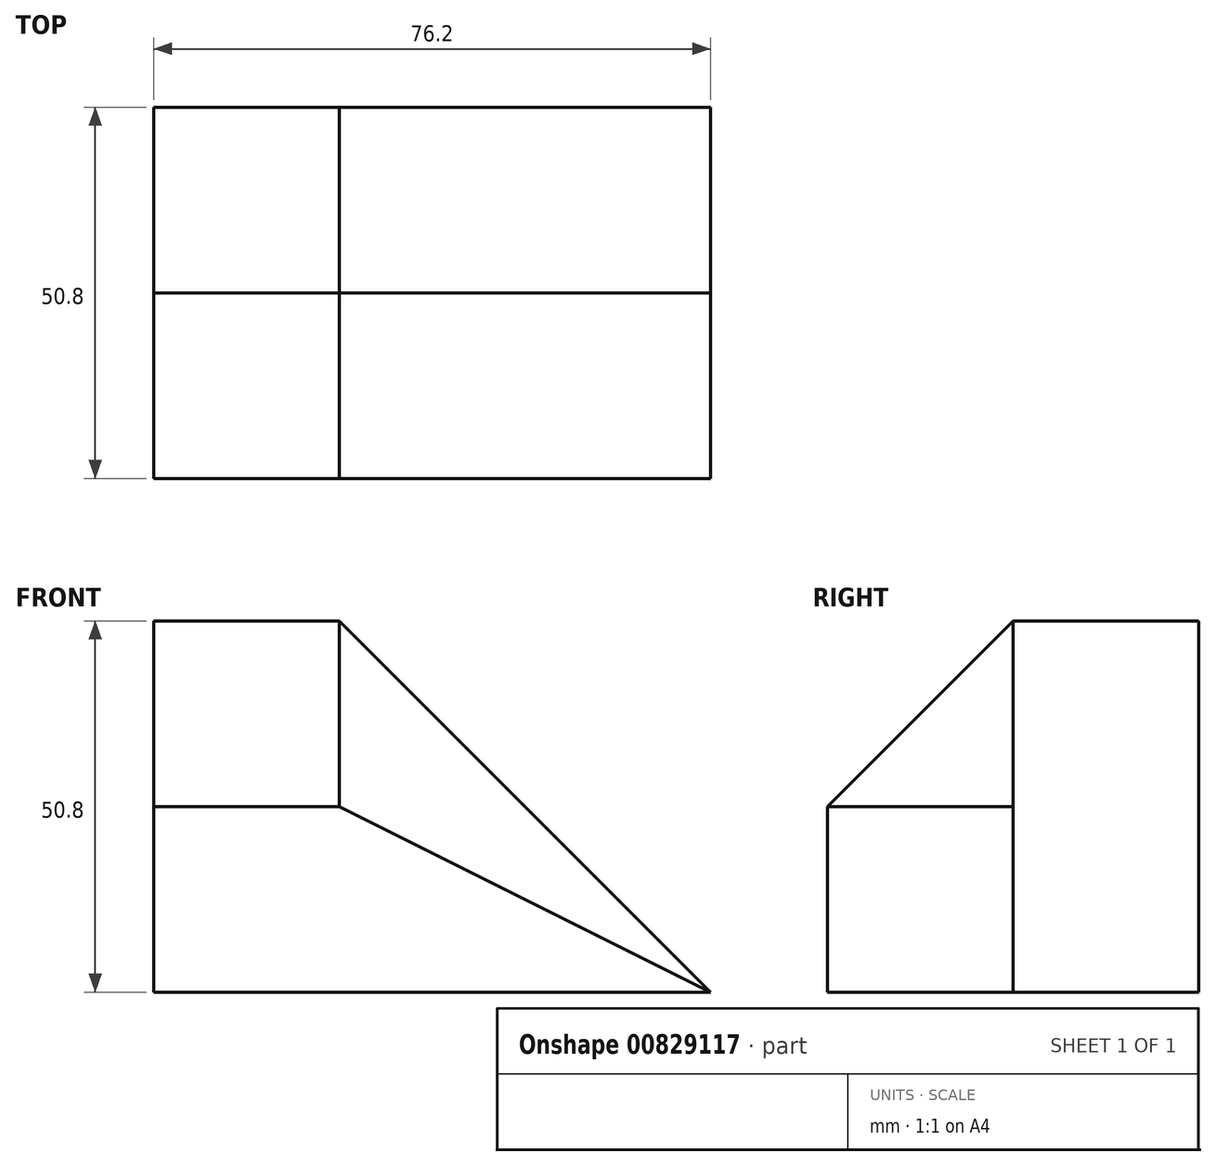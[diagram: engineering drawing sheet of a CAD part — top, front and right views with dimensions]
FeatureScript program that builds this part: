
annotation { "Feature Type Name" : "Feature", "Feature Type Description" : "" }
export const myFeature = defineFeature(function(context is Context, id is Id, definition is map)
    precondition{}
    {
        {
            var Q0;
            Q0=qCreatedBy(makeId("Front.planeOp"),FACE);
            var sketch = newSketch(context, id + "F0", { "sketchPlane" : qUnion([Q0])});
            skLineSegment(sketch, "E0", {"start": v(0, 0) * mm, "end": v(76.2, 0) * mm});
            skLineSegment(sketch, "E1", {"start": v(0, 0) * mm, "end": v(0, 50.8) * mm});
            skLineSegment(sketch, "E2", {"start": v(0, 50.8) * mm, "end": v(25.4, 50.8) * mm});
            skLineSegment(sketch, "E3", {"start": v(25.4, 50.8) * mm, "end": v(76.2, 0) * mm});
            skLineSegment(sketch, "E4", {"start": v(0, 25.4) * mm, "end": v(25.4, 25.4) * mm});
            skLineSegment(sketch, "E5", {"start": v(25.4, 25.4) * mm, "end": v(76.2, 0) * mm});
            skSolve(sketch);
        }
        {
            var Q0;
            {var subQ1=sQuery(id+"F0.wireOp",EDGE,"E2");Q0=makeQuery(id+"F0.imprint","IMPRINT",FACE,{"disambiguationData":[TD([[makeQuery(id+"F0.imprint","IMPRINT",EDGE,{"derivedFrom":subQ1}),-1.0]])]});}
            extrude(context, id + "F1", {"entities" : qUnion([Q0]), "depth" : 25.4 * mm, "offsetDistance" : 25.4 * mm});
        }
        {
            var Q0;
            {var subQ0=sQuery(id+"F0.wireOp",EDGE,"E0");Q0=makeQuery(id+"F0.imprint","IMPRINT",FACE,{"disambiguationData":[TD([[makeQuery(id+"F0.imprint","IMPRINT",EDGE,{"derivedFrom":subQ0}),1.0]])]});}
            extrude(context, id + "F2", {"entities" : qUnion([Q0]), "operationType" : NewBodyOperationType.ADD, "depth" : 50.8 * mm, "offsetDistance" : 25.4 * mm});
        }
        {
            var Q0;
            {var subQ0=sQuery(id+"F0.wireOp",EDGE,"E1");Q0=makeQuery(id+"F2.boolean.opBoolean","MERGE",FACE,{"derivedFrom":[makeQuery(id+"F1.opExtrude","SWEPT_FACE",FACE,{"disambiguationData":[OSD([subQ0])]}),makeQuery(id+"F2.opExtrude","SWEPT_FACE",FACE,{"disambiguationData":[OSD([subQ0])]})]});}
            var sketch = newSketch(context, id + "F3", { "sketchPlane" : qUnion([Q0])});
            skLineSegment(sketch, "E6", {"start": v(50.8, 25.4) * mm, "end": v(25.4, 50.8) * mm});
            skSolve(sketch);
        }
        {
            var Q0;
            Q0 = qSketchRegion(id + "F3", true);
            var Q1;
            Q1=makeQuery(id+"F3.imprint","IMPRINT",FACE,{"disambiguationData":[TD([[makeQuery(id+"F3.imprint","IMPRINT",EDGE,{"derivedFrom":sQuery(id+"F3.wireOp",EDGE,"E6")}),1.0]])]});
            extrude(context, id + "F4", {"entities" : qUnion([Q0, Q1]), "oppositeDirection" : true, "depth" : 25.4 * mm, "offsetDistance" : 25.4 * mm});
        }
    });
